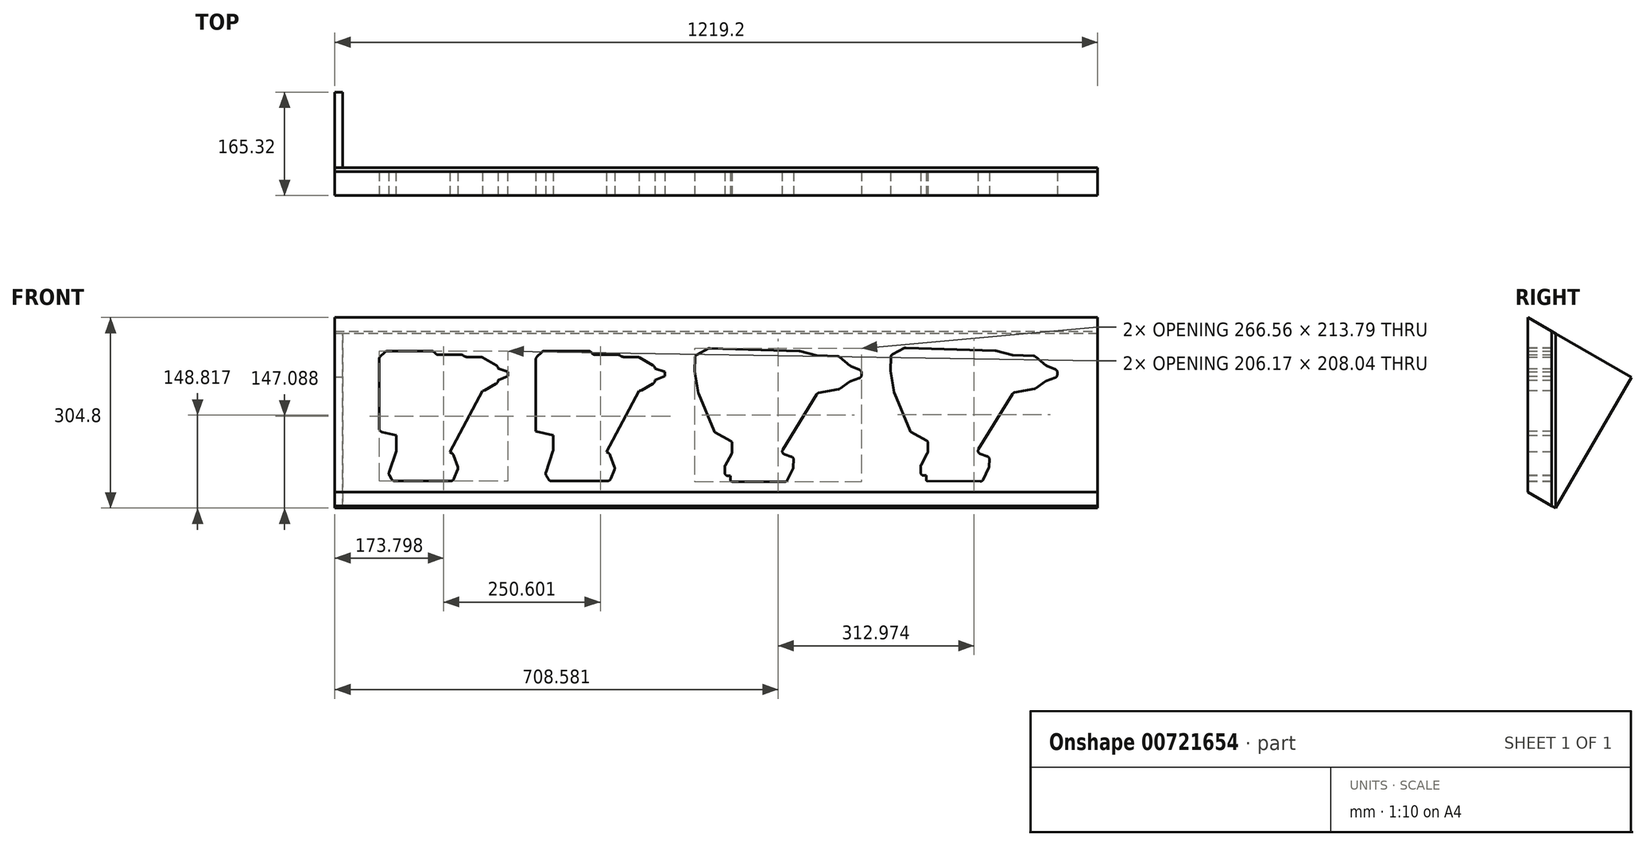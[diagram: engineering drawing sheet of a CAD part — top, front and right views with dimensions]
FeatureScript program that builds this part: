
annotation { "Feature Type Name" : "Feature", "Feature Type Description" : "" }
export const myFeature = defineFeature(function(context is Context, id is Id, definition is map)
    precondition{}
    {
        {
            var Q0;
            Q0=qCreatedBy(makeId("Front.planeOp"),FACE);
            var sketch = newSketch(context, id + "F0", { "sketchPlane" : qUnion([Q0])});
            skLineSegment(sketch, "E0", {"start": v(-3.88, -145.07) * mm, "end": v(92.56, -145.07) * mm});
            skLineSegment(sketch, "E1", {"start": v(92.56, -145.07) * mm, "end": v(100.9, -124.9) * mm});
            skLineSegment(sketch, "E2", {"start": v(100.9, -124.9) * mm, "end": v(92.56, -101.68) * mm});
            skLineSegment(sketch, "E3", {"start": v(92.56, -101.68) * mm, "end": v(82.48, -94.66) * mm});
            skLineSegment(sketch, "E4", {"start": v(82.48, -94.66) * mm, "end": v(58.37, -94.66) * mm});
            skLineSegment(sketch, "E5", {"start": v(58.37, -94.66) * mm, "end": v(63.63, -76.69) * mm});
            skLineSegment(sketch, "E6", {"start": v(63.63, -76.69) * mm, "end": v(66.7, -51.27) * mm});
            skLineSegment(sketch, "E7", {"start": v(66.7, -51.27) * mm, "end": v(92.56, -40.74) * mm});
            skLineSegment(sketch, "E8", {"start": v(92.56, -40.74) * mm, "end": v(88.62, -21.46) * mm});
            skLineSegment(sketch, "E9", {"start": v(88.62, -21.46) * mm, "end": v(105.71, -13.13) * mm});
            skLineSegment(sketch, "E10", {"start": v(105.71, -13.13) * mm, "end": v(112.29, -3.05) * mm});
            skLineSegment(sketch, "E11", {"start": v(112.29, -3.05) * mm, "end": v(141.66, -0.42) * mm});
            skLineSegment(sketch, "E12", {"start": v(141.66, -0.42) * mm, "end": v(164.84, 12.68) * mm});
            skLineSegment(sketch, "E13", {"start": v(164.84, 12.68) * mm, "end": v(164.84, 38.14) * mm});
            skLineSegment(sketch, "E14", {"start": v(164.84, 38.14) * mm, "end": v(138.25, 53.59) * mm});
            skLineSegment(sketch, "E15", {"start": v(138.25, 53.59) * mm, "end": v(112.38, 53.59) * mm});
            skLineSegment(sketch, "E16", {"start": v(112.38, 53.59) * mm, "end": v(107.55, 57) * mm});
            skLineSegment(sketch, "E17", {"start": v(107.55, 57) * mm, "end": v(65.77, 57) * mm});
            skLineSegment(sketch, "E18", {"start": v(65.77, 57) * mm, "end": v(61.79, 62.97) * mm});
            skLineSegment(sketch, "E19", {"start": v(61.79, 62.97) * mm, "end": v(-14.67, 62.97) * mm});
            skLineSegment(sketch, "E20", {"start": v(-14.67, 62.97) * mm, "end": v(-25.66, 51.99) * mm});
            skLineSegment(sketch, "E21", {"start": v(-25.66, 51.99) * mm, "end": v(-25.66, 17.9) * mm});
            skLineSegment(sketch, "E22", {"start": v(-25.66, 17.9) * mm, "end": v(-13.25, -15.48) * mm});
            skLineSegment(sketch, "E23", {"start": v(-13.25, -15.48) * mm, "end": v(10.62, -20.03) * mm});
            skLineSegment(sketch, "E24", {"start": v(10.62, -20.03) * mm, "end": v(5.27, -48.11) * mm});
            skLineSegment(sketch, "E25", {"start": v(5.27, -48.11) * mm, "end": v(2.1, -72.04) * mm});
            skLineSegment(sketch, "E26", {"start": v(2.1, -72.04) * mm, "end": v(2.1, -95.92) * mm});
            skLineSegment(sketch, "E27", {"start": v(2.1, -95.92) * mm, "end": v(-10.38, -133.46) * mm});
            skLineSegment(sketch, "E28", {"start": v(-10.38, -133.46) * mm, "end": v(-3.88, -145.07) * mm});
            skLineSegment(sketch, "E29.bottom", {"start": v(-96.37, 116.66) * mm, "end": v(1122.83, 116.66) * mm});
            skLineSegment(sketch, "E29.top", {"start": v(-96.37, -188.14) * mm, "end": v(1122.83, -188.14) * mm});
            skLineSegment(sketch, "E29.left", {"start": v(-96.37, 116.66) * mm, "end": v(-96.37, -188.14) * mm});
            skLineSegment(sketch, "E29.right", {"start": v(1122.83, 116.66) * mm, "end": v(1122.83, -188.14) * mm});
            skLineSegment(sketch, "E30", {"start": v(164.84, 35.17) * mm, "end": v(180.52, 29.83) * mm});
            skLineSegment(sketch, "E31", {"start": v(180.52, 29.83) * mm, "end": v(180.52, 22.7) * mm});
            skLineSegment(sketch, "E32", {"start": v(180.52, 22.7) * mm, "end": v(164.84, 16.26) * mm});
            skSolve(sketch);
        }
        {
            var Q0;
            Q0 = qSketchRegion(id + "F0", true);
            extrude(context, id + "F1", {"entities" : qUnion([Q0]), "depth" : 38.1 * mm, "offsetDistance" : 25.4 * mm});
        }
        {
            var Q0;
            Q0=makeQuery(id+"F1.opExtrude","SWEPT_EDGE",EDGE,{"disambiguationData":[OSD([sQuery(id+"F0.wireOp",EDGE,"E23"),sQuery(id+"F0.wireOp",EDGE,"E24")])]});
            var Q1;
            Q1=makeQuery(id+"F1.opExtrude","SWEPT_EDGE",EDGE,{"disambiguationData":[OSD([sQuery(id+"F0.wireOp",EDGE,"E22"),sQuery(id+"F0.wireOp",EDGE,"E23")])]});
            var Q2;
            Q2=makeQuery(id+"F1.opExtrude","SWEPT_EDGE",EDGE,{"disambiguationData":[OSD([sQuery(id+"F0.wireOp",EDGE,"E21"),sQuery(id+"F0.wireOp",EDGE,"E22")])]});
            var Q3;
            Q3=makeQuery(id+"F1.opExtrude","SWEPT_EDGE",EDGE,{"disambiguationData":[OSD([sQuery(id+"F0.wireOp",EDGE,"E20"),sQuery(id+"F0.wireOp",EDGE,"E21")])]});
            var Q4;
            Q4=makeQuery(id+"F1.opExtrude","SWEPT_EDGE",EDGE,{"disambiguationData":[OSD([sQuery(id+"F0.wireOp",EDGE,"E19"),sQuery(id+"F0.wireOp",EDGE,"E20")])]});
            var Q5;
            Q5=makeQuery(id+"F1.opExtrude","SWEPT_EDGE",EDGE,{"disambiguationData":[OSD([sQuery(id+"F0.wireOp",EDGE,"E18"),sQuery(id+"F0.wireOp",EDGE,"E19")])]});
            var Q6;
            Q6=makeQuery(id+"F1.opExtrude","SWEPT_EDGE",EDGE,{"disambiguationData":[OSD([sQuery(id+"F0.wireOp",EDGE,"E17"),sQuery(id+"F0.wireOp",EDGE,"E18")])]});
            var Q7;
            Q7=makeQuery(id+"F1.opExtrude","SWEPT_EDGE",EDGE,{"disambiguationData":[OSD([sQuery(id+"F0.wireOp",EDGE,"E16"),sQuery(id+"F0.wireOp",EDGE,"E17")])]});
            var Q8;
            Q8=makeQuery(id+"F1.opExtrude","SWEPT_EDGE",EDGE,{"disambiguationData":[OSD([sQuery(id+"F0.wireOp",EDGE,"E15"),sQuery(id+"F0.wireOp",EDGE,"E16")])]});
            var Q9;
            Q9=makeQuery(id+"F1.opExtrude","SWEPT_EDGE",EDGE,{"disambiguationData":[OSD([sQuery(id+"F0.wireOp",EDGE,"E14"),sQuery(id+"F0.wireOp",EDGE,"E15")])]});
            var Q10;
            Q10=makeQuery(id+"F1.opExtrude","SWEPT_EDGE",EDGE,{"disambiguationData":[OSD([sQuery(id+"F0.wireOp",EDGE,"E13"),sQuery(id+"F0.wireOp",EDGE,"E14")])]});
            var Q11;
            Q11=makeQuery(id+"F1.opExtrude","SWEPT_EDGE",EDGE,{"disambiguationData":[OSD([sQuery(id+"F0.wireOp",EDGE,"E12"),sQuery(id+"F0.wireOp",EDGE,"E13")])]});
            var Q12;
            Q12=makeQuery(id+"F1.opExtrude","SWEPT_EDGE",EDGE,{"disambiguationData":[OSD([sQuery(id+"F0.wireOp",EDGE,"E11"),sQuery(id+"F0.wireOp",EDGE,"E12")])]});
            var Q13;
            Q13=makeQuery(id+"F1.opExtrude","SWEPT_EDGE",EDGE,{"disambiguationData":[OSD([sQuery(id+"F0.wireOp",EDGE,"E10"),sQuery(id+"F0.wireOp",EDGE,"E11")])]});
            var Q14;
            Q14=makeQuery(id+"F1.opExtrude","SWEPT_EDGE",EDGE,{"disambiguationData":[OSD([sQuery(id+"F0.wireOp",EDGE,"E9"),sQuery(id+"F0.wireOp",EDGE,"E10")])]});
            var Q15;
            Q15=makeQuery(id+"F1.opExtrude","SWEPT_EDGE",EDGE,{"disambiguationData":[OSD([sQuery(id+"F0.wireOp",EDGE,"E8"),sQuery(id+"F0.wireOp",EDGE,"E9")])]});
            var Q16;
            Q16=makeQuery(id+"F1.opExtrude","SWEPT_EDGE",EDGE,{"disambiguationData":[OSD([sQuery(id+"F0.wireOp",EDGE,"E7"),sQuery(id+"F0.wireOp",EDGE,"E8")])]});
            var Q17;
            Q17=makeQuery(id+"F1.opExtrude","SWEPT_EDGE",EDGE,{"disambiguationData":[OSD([sQuery(id+"F0.wireOp",EDGE,"E6"),sQuery(id+"F0.wireOp",EDGE,"E7")])]});
            var Q18;
            Q18=makeQuery(id+"F1.opExtrude","SWEPT_EDGE",EDGE,{"disambiguationData":[OSD([sQuery(id+"F0.wireOp",EDGE,"E5"),sQuery(id+"F0.wireOp",EDGE,"E6")])]});
            var Q19;
            Q19=makeQuery(id+"F1.opExtrude","SWEPT_EDGE",EDGE,{"disambiguationData":[OSD([sQuery(id+"F0.wireOp",EDGE,"E4"),sQuery(id+"F0.wireOp",EDGE,"E5")])]});
            var Q20;
            Q20=makeQuery(id+"F1.opExtrude","SWEPT_EDGE",EDGE,{"disambiguationData":[OSD([sQuery(id+"F0.wireOp",EDGE,"E2"),sQuery(id+"F0.wireOp",EDGE,"E3")])]});
            var Q21;
            Q21=makeQuery(id+"F1.opExtrude","SWEPT_EDGE",EDGE,{"disambiguationData":[OSD([sQuery(id+"F0.wireOp",EDGE,"E1"),sQuery(id+"F0.wireOp",EDGE,"E2")])]});
            var Q22;
            Q22=makeQuery(id+"F1.opExtrude","SWEPT_EDGE",EDGE,{"disambiguationData":[OSD([sQuery(id+"F0.wireOp",EDGE,"E3"),sQuery(id+"F0.wireOp",EDGE,"E4")])]});
            var Q23;
            Q23=makeQuery(id+"F1.opExtrude","SWEPT_EDGE",EDGE,{"disambiguationData":[OSD([sQuery(id+"F0.wireOp",EDGE,"E0"),sQuery(id+"F0.wireOp",EDGE,"E1")])]});
            var Q24;
            Q24=makeQuery(id+"F1.opExtrude","SWEPT_EDGE",EDGE,{"disambiguationData":[OSD([sQuery(id+"F0.wireOp",EDGE,"E0"),sQuery(id+"F0.wireOp",EDGE,"E28")])]});
            var Q25;
            Q25=makeQuery(id+"F1.opExtrude","SWEPT_EDGE",EDGE,{"disambiguationData":[OSD([sQuery(id+"F0.wireOp",EDGE,"E27"),sQuery(id+"F0.wireOp",EDGE,"E28")])]});
            var Q26;
            Q26=makeQuery(id+"F1.opExtrude","SWEPT_EDGE",EDGE,{"disambiguationData":[OSD([sQuery(id+"F0.wireOp",EDGE,"E26"),sQuery(id+"F0.wireOp",EDGE,"E27")])]});
            var Q27;
            Q27=makeQuery(id+"F1.opExtrude","SWEPT_EDGE",EDGE,{"disambiguationData":[OSD([sQuery(id+"F0.wireOp",EDGE,"E25"),sQuery(id+"F0.wireOp",EDGE,"E26")])]});
            var Q28;
            Q28=makeQuery(id+"F1.opExtrude","SWEPT_EDGE",EDGE,{"disambiguationData":[OSD([sQuery(id+"F0.wireOp",EDGE,"E24"),sQuery(id+"F0.wireOp",EDGE,"E25")])]});
            fillet(context, id + "F2", {"entities" : qUnion([Q0, Q1, Q2, Q3, Q4, Q5, Q6, Q7, Q8, Q9, Q10, Q11, Q12, Q13, Q14, Q15, Q16, Q17, Q18, Q19, Q20, Q21, Q22, Q23, Q24, Q25, Q26, Q27, Q28]), "radius" : 6.35 * mm, "tangentPropagation" : true, "allowEdgeOverflow" : false});
        }
        {
            var Q0;
            Q0=makeQuery(id+"F1.opExtrude","CAP_FACE",FACE,{"disambiguationData":[OSD([sQuery(id+"F0.wireOp",EDGE,"E0"),sQuery(id+"F0.wireOp",EDGE,"E1"),sQuery(id+"F0.wireOp",EDGE,"E2"),sQuery(id+"F0.wireOp",EDGE,"E3"),sQuery(id+"F0.wireOp",EDGE,"E4"),sQuery(id+"F0.wireOp",EDGE,"E5"),sQuery(id+"F0.wireOp",EDGE,"E6"),sQuery(id+"F0.wireOp",EDGE,"E7"),sQuery(id+"F0.wireOp",EDGE,"E8"),sQuery(id+"F0.wireOp",EDGE,"E9"),sQuery(id+"F0.wireOp",EDGE,"E10"),sQuery(id+"F0.wireOp",EDGE,"E11"),sQuery(id+"F0.wireOp",EDGE,"E12"),sQuery(id+"F0.wireOp",EDGE,"E13"),sQuery(id+"F0.wireOp",EDGE,"E14"),sQuery(id+"F0.wireOp",EDGE,"E15"),sQuery(id+"F0.wireOp",EDGE,"E16"),sQuery(id+"F0.wireOp",EDGE,"E17"),sQuery(id+"F0.wireOp",EDGE,"E18"),sQuery(id+"F0.wireOp",EDGE,"E19"),sQuery(id+"F0.wireOp",EDGE,"E20"),sQuery(id+"F0.wireOp",EDGE,"E21"),sQuery(id+"F0.wireOp",EDGE,"E22"),sQuery(id+"F0.wireOp",EDGE,"E23"),sQuery(id+"F0.wireOp",EDGE,"E24"),sQuery(id+"F0.wireOp",EDGE,"E25"),sQuery(id+"F0.wireOp",EDGE,"E26"),sQuery(id+"F0.wireOp",EDGE,"E27"),sQuery(id+"F0.wireOp",EDGE,"E28"),sQuery(id+"F0.wireOp",EDGE,"E29.bottom"),sQuery(id+"F0.wireOp",EDGE,"E29.top"),sQuery(id+"F0.wireOp",EDGE,"E29.left"),sQuery(id+"F0.wireOp",EDGE,"E29.right")])],"isStart":false});
            var sketch = newSketch(context, id + "F3", { "sketchPlane" : qUnion([Q0])});
            skLineSegment(sketch, "E33", {"start": v(-25.66, 19.04) * mm, "end": v(-25.66, -65.36) * mm});
            skLineSegment(sketch, "E34", {"start": v(87.5, -98.16) * mm, "end": v(139.63, -0.6) * mm});
            skLineSegment(sketch, "E35.0", {"start": v(-0.16, -145.07) * mm, "end": v(88.31, -145.07) * mm});
            skArc(sketch, "E35.1", {"start": v(-0.16, -145.07) * mm, "mid": v(-3.37, -144.2) * mm, "end": v(-5.7, -141.83) * mm});
            skLineSegment(sketch, "E35.2", {"start": v(-9, -135.9) * mm, "end": v(-5.7, -141.83) * mm});
            skArc(sketch, "E35.3", {"start": v(-9, -135.9) * mm, "mid": v(-9.8, -133.4) * mm, "end": v(-9.5, -130.8) * mm});
            skLineSegment(sketch, "E35.4", {"start": v(1.77, -96.9) * mm, "end": v(-9.5, -130.8) * mm});
            skArc(sketch, "E35.5", {"start": v(94.18, -141.15) * mm, "mid": v(91.84, -144) * mm, "end": v(88.31, -145.07) * mm});
            skLineSegment(sketch, "E35.6", {"start": v(94.18, -141.15) * mm, "end": v(99.96, -127.17) * mm});
            skArc(sketch, "E35.7", {"start": v(100.06, -122.6) * mm, "mid": v(100.44, -124.9) * mm, "end": v(99.96, -127.17) * mm});
            skLineSegment(sketch, "E35.8", {"start": v(100.06, -122.6) * mm, "end": v(93.25, -103.59) * mm});
            skLineSegment(sketch, "E35.9", {"start": v(90.9, -100.52) * mm, "end": v(87.5, -98.16) * mm});
            skArc(sketch, "E35.10", {"start": v(90.9, -100.52) * mm, "mid": v(92.31, -101.87) * mm, "end": v(93.25, -103.59) * mm});
            skLineSegment(sketch, "E35.12", {"start": v(2.1, -72.46) * mm, "end": v(2.1, -94.9) * mm});
            skLineSegment(sketch, "E35.13", {"start": v(142.85, 0.26) * mm, "end": v(161.61, 10.85) * mm});
            skArc(sketch, "E35.14", {"start": v(164.84, 16.26) * mm, "mid": v(163.95, 13.13) * mm, "end": v(161.61, 10.85) * mm});
            skLineSegment(sketch, "E35.15", {"start": v(180.52, 22.7) * mm, "end": v(164.84, 16.26) * mm});
            skLineSegment(sketch, "E35.16", {"start": v(180.52, 29.83) * mm, "end": v(180.52, 22.7) * mm});
            skLineSegment(sketch, "E35.17", {"start": v(164.84, 35.17) * mm, "end": v(180.52, 29.83) * mm});
            skArc(sketch, "E35.18", {"start": v(161.72, 39.96) * mm, "mid": v(163.85, 37.93) * mm, "end": v(164.84, 35.17) * mm});
            skLineSegment(sketch, "E35.19", {"start": v(161.72, 39.96) * mm, "end": v(139.73, 52.73) * mm});
            skArc(sketch, "E35.20", {"start": v(136.54, 53.59) * mm, "mid": v(138.19, 53.37) * mm, "end": v(139.73, 52.73) * mm});
            skLineSegment(sketch, "E35.21", {"start": v(136.54, 53.59) * mm, "end": v(114.4, 53.59) * mm});
            skArc(sketch, "E35.22", {"start": v(110.73, 54.75) * mm, "mid": v(112.48, 53.89) * mm, "end": v(114.4, 53.59) * mm});
            skLineSegment(sketch, "E35.23", {"start": v(110.73, 54.75) * mm, "end": v(109.2, 55.84) * mm});
            skArc(sketch, "E35.24", {"start": v(105.53, 57) * mm, "mid": v(107.45, 56.7) * mm, "end": v(109.2, 55.84) * mm});
            skLineSegment(sketch, "E35.26", {"start": v(105.53, 57) * mm, "end": v(69.16, 57) * mm});
            skPoint(sketch, "E35.27", {"position": v(92.31, -101.87) * mm});
            skArc(sketch, "E36.0", {"start": v(63.88, 59.83) * mm, "mid": v(66.17, 57.75) * mm, "end": v(69.16, 57) * mm});
            skArc(sketch, "E36.1", {"start": v(58.39, 62.97) * mm, "mid": v(61.38, 62.22) * mm, "end": v(63.67, 60.14) * mm});
            skLineSegment(sketch, "E36.2", {"start": v(58.39, 62.97) * mm, "end": v(-12.04, 62.97) * mm});
            skPoint(sketch, "E36.3", {"position": v(-16.53, 61.1) * mm});
            skLineSegment(sketch, "E36.4", {"start": v(-16.53, 61.1) * mm, "end": v(-23.8, 53.85) * mm});
            skArc(sketch, "E36.5", {"start": v(-16.53, 61.1) * mm, "mid": v(-14.47, 62.49) * mm, "end": v(-12.04, 62.97) * mm});
            skLineSegment(sketch, "E36.6", {"start": v(-25.66, 49.35) * mm, "end": v(-25.66, 19.04) * mm});
            skArc(sketch, "E36.7", {"start": v(-25.66, 49.35) * mm, "mid": v(-25.18, 51.78) * mm, "end": v(-23.8, 53.85) * mm});
            skPoint(sketch, "E37.orphan", {"position": v(84.11, -95.8) * mm});
            skLineSegment(sketch, "E38", {"start": v(2.15, -71.63) * mm, "end": v(-25.66, -65.36) * mm});
            skPoint(sketch, "E39.0", {"position": v(2.01, -95.9) * mm});
            skArc(sketch, "E40.0", {"start": v(1.77, -96.9) * mm, "mid": v(2.01, -95.9) * mm, "end": v(2.1, -94.9) * mm});
            skArc(sketch, "E41.2", {"start": v(2.1, -72.46) * mm, "mid": v(2.1, -72.05) * mm, "end": v(2.15, -71.63) * mm});
            skArc(sketch, "E42.0", {"start": v(142.85, 0.26) * mm, "mid": v(141.61, -0.28) * mm, "end": v(140.3, -0.54) * mm});
            skLineSegment(sketch, "E42.1", {"start": v(139.63, -0.6) * mm, "end": v(140.3, -0.54) * mm});
            skPoint(sketch, "E43.orphan", {"position": v(115.36, -2.77) * mm});
            skLineSegment(sketch, "E44.0", {"start": v(63.88, 59.83) * mm, "end": v(63.67, 60.14) * mm});
            skLineSegment(sketch, "E45", {"start": v(-85.76, -145.07) * mm, "end": v(1133.44, -145.07) * mm, "construction": true});
            skLineSegment(sketch, "E46", {"start": v(224.94, 19.04) * mm, "end": v(224.94, -65.36) * mm});
            skLineSegment(sketch, "E47", {"start": v(338.1, -98.16) * mm, "end": v(390.23, -0.6) * mm});
            skLineSegment(sketch, "E48.0", {"start": v(250.45, -145.07) * mm, "end": v(338.91, -145.07) * mm});
            skArc(sketch, "E48.1", {"start": v(250.45, -145.07) * mm, "mid": v(247.23, -144.2) * mm, "end": v(244.9, -141.83) * mm});
            skLineSegment(sketch, "E48.2", {"start": v(241.6, -135.9) * mm, "end": v(244.9, -141.83) * mm});
            skArc(sketch, "E48.3", {"start": v(241.6, -135.9) * mm, "mid": v(240.8, -133.4) * mm, "end": v(241.1, -130.8) * mm});
            skLineSegment(sketch, "E48.4", {"start": v(252.37, -96.9) * mm, "end": v(241.1, -130.8) * mm});
            skArc(sketch, "E48.5", {"start": v(344.78, -141.15) * mm, "mid": v(342.45, -144) * mm, "end": v(338.91, -145.07) * mm});
            skLineSegment(sketch, "E48.6", {"start": v(344.78, -141.15) * mm, "end": v(350.56, -127.17) * mm});
            skArc(sketch, "E48.7", {"start": v(350.66, -122.6) * mm, "mid": v(351.04, -124.9) * mm, "end": v(350.56, -127.17) * mm});
            skLineSegment(sketch, "E48.8", {"start": v(350.66, -122.6) * mm, "end": v(343.85, -103.59) * mm});
            skLineSegment(sketch, "E48.9", {"start": v(341.5, -100.52) * mm, "end": v(338.1, -98.16) * mm});
            skArc(sketch, "E48.10", {"start": v(341.5, -100.52) * mm, "mid": v(342.91, -101.87) * mm, "end": v(343.85, -103.59) * mm});
            skLineSegment(sketch, "E48.12", {"start": v(252.7, -72.46) * mm, "end": v(252.7, -94.9) * mm});
            skLineSegment(sketch, "E48.13", {"start": v(393.45, 0.26) * mm, "end": v(412.22, 10.85) * mm});
            skArc(sketch, "E48.14", {"start": v(415.44, 16.26) * mm, "mid": v(414.55, 13.13) * mm, "end": v(412.22, 10.85) * mm});
            skLineSegment(sketch, "E48.15", {"start": v(431.12, 22.7) * mm, "end": v(415.44, 16.26) * mm});
            skLineSegment(sketch, "E48.16", {"start": v(431.12, 29.83) * mm, "end": v(431.12, 22.7) * mm});
            skLineSegment(sketch, "E48.17", {"start": v(415.44, 35.17) * mm, "end": v(431.12, 29.83) * mm});
            skArc(sketch, "E48.18", {"start": v(412.32, 39.96) * mm, "mid": v(414.45, 37.93) * mm, "end": v(415.44, 35.17) * mm});
            skLineSegment(sketch, "E48.19", {"start": v(412.32, 39.96) * mm, "end": v(390.33, 52.73) * mm});
            skArc(sketch, "E48.20", {"start": v(387.14, 53.59) * mm, "mid": v(388.79, 53.37) * mm, "end": v(390.33, 52.73) * mm});
            skLineSegment(sketch, "E48.21", {"start": v(387.14, 53.59) * mm, "end": v(365, 53.59) * mm});
            skArc(sketch, "E48.22", {"start": v(361.33, 54.75) * mm, "mid": v(363.08, 53.89) * mm, "end": v(365, 53.59) * mm});
            skLineSegment(sketch, "E48.23", {"start": v(361.33, 54.75) * mm, "end": v(359.8, 55.84) * mm});
            skArc(sketch, "E48.24", {"start": v(356.13, 57) * mm, "mid": v(358.05, 56.7) * mm, "end": v(359.8, 55.84) * mm});
            skLineSegment(sketch, "E48.26", {"start": v(356.13, 57) * mm, "end": v(319.76, 57) * mm});
            skPoint(sketch, "E48.27", {"position": v(342.9, -101.87) * mm});
            skArc(sketch, "E49.0", {"start": v(314.48, 59.83) * mm, "mid": v(316.77, 57.75) * mm, "end": v(319.76, 57) * mm});
            skArc(sketch, "E49.1", {"start": v(308.99, 62.97) * mm, "mid": v(311.98, 62.22) * mm, "end": v(314.27, 60.14) * mm});
            skLineSegment(sketch, "E49.2", {"start": v(308.99, 62.97) * mm, "end": v(238.56, 62.97) * mm});
            skPoint(sketch, "E49.3", {"position": v(234.07, 61.1) * mm});
            skLineSegment(sketch, "E49.4", {"start": v(234.07, 61.1) * mm, "end": v(226.8, 53.85) * mm});
            skArc(sketch, "E49.5", {"start": v(234.07, 61.1) * mm, "mid": v(236.13, 62.49) * mm, "end": v(238.56, 62.97) * mm});
            skLineSegment(sketch, "E49.6", {"start": v(224.94, 49.35) * mm, "end": v(224.94, 19.04) * mm});
            skArc(sketch, "E49.7", {"start": v(224.94, 49.35) * mm, "mid": v(225.43, 51.79) * mm, "end": v(226.8, 53.85) * mm});
            skPoint(sketch, "E50.orphan", {"position": v(334.71, -95.8) * mm});
            skLineSegment(sketch, "E51", {"start": v(252.75, -71.63) * mm, "end": v(224.94, -65.36) * mm});
            skPoint(sketch, "E52.0", {"position": v(252.61, -95.9) * mm});
            skArc(sketch, "E53.0", {"start": v(252.37, -96.9) * mm, "mid": v(252.61, -95.9) * mm, "end": v(252.7, -94.9) * mm});
            skArc(sketch, "E54.2", {"start": v(252.7, -72.46) * mm, "mid": v(252.71, -72.05) * mm, "end": v(252.75, -71.63) * mm});
            skArc(sketch, "E55.0", {"start": v(393.45, 0.26) * mm, "mid": v(392.21, -0.28) * mm, "end": v(390.9, -0.54) * mm});
            skLineSegment(sketch, "E55.1", {"start": v(390.23, -0.6) * mm, "end": v(390.9, -0.54) * mm});
            skPoint(sketch, "E56.orphan", {"position": v(365.96, -2.77) * mm});
            skLineSegment(sketch, "E57.0", {"start": v(314.48, 59.83) * mm, "end": v(314.27, 60.14) * mm});
            skLineSegment(sketch, "E58.1", {"start": v(503.42, 67.57) * mm, "end": v(645.87, 62.84) * mm});
            skArc(sketch, "E58.2", {"start": v(500.9, 67) * mm, "mid": v(502.12, 67.45) * mm, "end": v(503.42, 67.57) * mm});
            skLineSegment(sketch, "E58.3", {"start": v(482.38, 57.35) * mm, "end": v(500.9, 67) * mm});
            skArc(sketch, "E58.4", {"start": v(479.65, 53.02) * mm, "mid": v(480.43, 55.56) * mm, "end": v(482.38, 57.35) * mm});
            skLineSegment(sketch, "E58.5", {"start": v(478.93, 31.35) * mm, "end": v(479.65, 53.02) * mm});
            skLineSegment(sketch, "E58.6", {"start": v(646.97, 62.69) * mm, "end": v(673.62, 55.83) * mm});
            skArc(sketch, "E58.7", {"start": v(645.87, 62.84) * mm, "mid": v(646.42, 62.8) * mm, "end": v(646.97, 62.69) * mm});
            skArc(sketch, "E58.8", {"start": v(673.62, 55.83) * mm, "mid": v(674.16, 55.72) * mm, "end": v(674.71, 55.67) * mm});
            skLineSegment(sketch, "E58.9", {"start": v(674.71, 55.67) * mm, "end": v(707.37, 54.59) * mm});
            skArc(sketch, "E58.10", {"start": v(707.37, 54.59) * mm, "mid": v(708.98, 54.27) * mm, "end": v(710.4, 53.45) * mm});
            skLineSegment(sketch, "E58.11", {"start": v(710.4, 53.45) * mm, "end": v(727.44, 39.6) * mm});
            skArc(sketch, "E58.12", {"start": v(727.44, 39.6) * mm, "mid": v(728.01, 39.19) * mm, "end": v(728.64, 38.87) * mm});
            skLineSegment(sketch, "E58.13", {"start": v(728.64, 38.87) * mm, "end": v(742.42, 32.94) * mm});
            skArc(sketch, "E58.14", {"start": v(742.42, 32.94) * mm, "mid": v(744.7, 31) * mm, "end": v(745.49, 28.1) * mm});
            skLineSegment(sketch, "E58.15", {"start": v(745.49, 28.1) * mm, "end": v(745.36, 24.17) * mm});
            skArc(sketch, "E58.16", {"start": v(745.36, 24.17) * mm, "mid": v(744.38, 21.34) * mm, "end": v(741.98, 19.55) * mm});
            skLineSegment(sketch, "E58.17", {"start": v(741.98, 19.55) * mm, "end": v(727.83, 14.55) * mm});
            skArc(sketch, "E58.18", {"start": v(727.83, 14.55) * mm, "mid": v(727.19, 14.27) * mm, "end": v(726.59, 13.9) * mm});
            skLineSegment(sketch, "E58.19", {"start": v(726.59, 13.9) * mm, "end": v(710.58, 2.57) * mm});
            skArc(sketch, "E58.20", {"start": v(710.58, 2.57) * mm, "mid": v(709.61, 2.03) * mm, "end": v(708.56, 1.71) * mm});
            skLineSegment(sketch, "E58.21", {"start": v(708.56, 1.71) * mm, "end": v(677.11, -4.02) * mm});
            skArc(sketch, "E58.22", {"start": v(677.11, -4.02) * mm, "mid": v(675.15, -4.83) * mm, "end": v(673.7, -6.36) * mm});
            skLineSegment(sketch, "E58.23", {"start": v(619.56, -94.7) * mm, "end": v(673.7, -6.36) * mm});
            skArc(sketch, "E58.24", {"start": v(619.56, -94.7) * mm, "mid": v(619.12, -99.1) * mm, "end": v(622.28, -102.18) * mm});
            skLineSegment(sketch, "E58.25", {"start": v(622.28, -102.18) * mm, "end": v(633.44, -105.92) * mm});
            skArc(sketch, "E58.26", {"start": v(633.44, -105.92) * mm, "mid": v(636, -107.83) * mm, "end": v(636.9, -110.9) * mm});
            skLineSegment(sketch, "E58.27", {"start": v(636.9, -110.9) * mm, "end": v(636.53, -122.23) * mm});
            skLineSegment(sketch, "E58.28", {"start": v(636.03, -124.25) * mm, "end": v(626.9, -143.33) * mm});
            skArc(sketch, "E58.29", {"start": v(636.53, -122.23) * mm, "mid": v(636.39, -123.27) * mm, "end": v(636.03, -124.25) * mm});
            skArc(sketch, "E58.30", {"start": v(626.9, -143.33) * mm, "mid": v(625.01, -145.44) * mm, "end": v(622.29, -146.22) * mm});
            skLineSegment(sketch, "E58.31", {"start": v(622.29, -146.22) * mm, "end": v(538.27, -145.73) * mm});
            skArc(sketch, "E58.32", {"start": v(538.27, -145.73) * mm, "mid": v(536.75, -145.1) * mm, "end": v(536.13, -143.56) * mm});
            skLineSegment(sketch, "E58.33", {"start": v(536.13, -143.56) * mm, "end": v(536.17, -136.78) * mm});
            skLineSegment(sketch, "E58.34", {"start": v(536.17, -136.78) * mm, "end": v(532, -136.76) * mm});
            skArc(sketch, "E58.35", {"start": v(532, -136.76) * mm, "mid": v(528.41, -135.25) * mm, "end": v(526.95, -131.65) * mm});
            skLineSegment(sketch, "E58.36", {"start": v(526.95, -131.65) * mm, "end": v(527, -122.17) * mm});
            skArc(sketch, "E58.37", {"start": v(527, -122.17) * mm, "mid": v(527.17, -120.9) * mm, "end": v(527.64, -119.72) * mm});
            skLineSegment(sketch, "E58.38", {"start": v(527.64, -119.72) * mm, "end": v(537.65, -101.75) * mm});
            skArc(sketch, "E58.39", {"start": v(537.65, -101.75) * mm, "mid": v(538.1, -100.64) * mm, "end": v(538.29, -99.45) * mm});
            skLineSegment(sketch, "E58.40", {"start": v(538.29, -99.45) * mm, "end": v(538.76, -85.12) * mm});
            skArc(sketch, "E58.41", {"start": v(538.76, -85.12) * mm, "mid": v(538.09, -82.43) * mm, "end": v(536.1, -80.49) * mm});
            skLineSegment(sketch, "E58.42", {"start": v(536.1, -80.49) * mm, "end": v(512.08, -67.51) * mm});
            skArc(sketch, "E58.43", {"start": v(512.08, -67.51) * mm, "mid": v(510.72, -66.45) * mm, "end": v(509.8, -64.99) * mm});
            skLineSegment(sketch, "E58.44", {"start": v(509.8, -64.99) * mm, "end": v(485.02, -5.14) * mm});
            skLineSegment(sketch, "E58.45", {"start": v(484.7, -4.03) * mm, "end": v(479, 30.36) * mm});
            skArc(sketch, "E58.46", {"start": v(485.02, -5.14) * mm, "mid": v(484.83, -4.6) * mm, "end": v(484.7, -4.03) * mm});
            skArc(sketch, "E58.47", {"start": v(479, 30.36) * mm, "mid": v(478.94, 30.85) * mm, "end": v(478.93, 31.35) * mm});
            skPoint(sketch, "E58.48", {"position": v(636.39, -123.27) * mm});
            skLineSegment(sketch, "E59.1", {"start": v(816.4, 68.23) * mm, "end": v(958.84, 63.5) * mm});
            skArc(sketch, "E59.2", {"start": v(813.88, 67.66) * mm, "mid": v(815.1, 68.1) * mm, "end": v(816.4, 68.23) * mm});
            skLineSegment(sketch, "E59.3", {"start": v(795.36, 58.01) * mm, "end": v(813.88, 67.66) * mm});
            skArc(sketch, "E59.4", {"start": v(792.63, 53.68) * mm, "mid": v(793.4, 56.22) * mm, "end": v(795.36, 58.01) * mm});
            skLineSegment(sketch, "E59.5", {"start": v(791.9, 32.01) * mm, "end": v(792.63, 53.68) * mm});
            skLineSegment(sketch, "E59.6", {"start": v(959.94, 63.35) * mm, "end": v(986.6, 56.49) * mm});
            skArc(sketch, "E59.7", {"start": v(958.84, 63.5) * mm, "mid": v(959.4, 63.46) * mm, "end": v(959.94, 63.35) * mm});
            skArc(sketch, "E59.8", {"start": v(986.6, 56.49) * mm, "mid": v(987.13, 56.38) * mm, "end": v(987.69, 56.33) * mm});
            skLineSegment(sketch, "E59.9", {"start": v(987.69, 56.33) * mm, "end": v(1020.34, 55.25) * mm});
            skArc(sketch, "E59.10", {"start": v(1020.34, 55.25) * mm, "mid": v(1021.95, 54.93) * mm, "end": v(1023.38, 54.11) * mm});
            skLineSegment(sketch, "E59.11", {"start": v(1023.38, 54.11) * mm, "end": v(1040.41, 40.25) * mm});
            skArc(sketch, "E59.12", {"start": v(1040.41, 40.25) * mm, "mid": v(1040.99, 39.85) * mm, "end": v(1041.61, 39.53) * mm});
            skLineSegment(sketch, "E59.13", {"start": v(1041.61, 39.53) * mm, "end": v(1055.4, 33.6) * mm});
            skArc(sketch, "E59.14", {"start": v(1055.4, 33.6) * mm, "mid": v(1057.68, 31.65) * mm, "end": v(1058.46, 28.76) * mm});
            skLineSegment(sketch, "E59.15", {"start": v(1058.46, 28.76) * mm, "end": v(1058.33, 24.83) * mm});
            skArc(sketch, "E59.16", {"start": v(1058.33, 24.83) * mm, "mid": v(1057.36, 22) * mm, "end": v(1054.95, 20.2) * mm});
            skLineSegment(sketch, "E59.17", {"start": v(1054.95, 20.2) * mm, "end": v(1040.8, 15.2) * mm});
            skArc(sketch, "E59.18", {"start": v(1040.8, 15.2) * mm, "mid": v(1040.16, 14.93) * mm, "end": v(1039.56, 14.56) * mm});
            skLineSegment(sketch, "E59.19", {"start": v(1039.56, 14.56) * mm, "end": v(1023.55, 3.23) * mm});
            skArc(sketch, "E59.20", {"start": v(1023.55, 3.23) * mm, "mid": v(1022.59, 2.69) * mm, "end": v(1021.53, 2.37) * mm});
            skLineSegment(sketch, "E59.21", {"start": v(1021.53, 2.37) * mm, "end": v(990.09, -3.36) * mm});
            skArc(sketch, "E59.22", {"start": v(990.09, -3.36) * mm, "mid": v(988.13, -4.17) * mm, "end": v(986.67, -5.7) * mm});
            skLineSegment(sketch, "E59.23", {"start": v(932.53, -94.05) * mm, "end": v(986.67, -5.7) * mm});
            skArc(sketch, "E59.24", {"start": v(932.53, -94.05) * mm, "mid": v(932.1, -98.44) * mm, "end": v(935.25, -101.52) * mm});
            skLineSegment(sketch, "E59.25", {"start": v(935.25, -101.52) * mm, "end": v(946.42, -105.26) * mm});
            skArc(sketch, "E59.26", {"start": v(946.42, -105.26) * mm, "mid": v(948.97, -107.17) * mm, "end": v(949.88, -110.24) * mm});
            skLineSegment(sketch, "E59.27", {"start": v(949.88, -110.24) * mm, "end": v(949.5, -121.57) * mm});
            skLineSegment(sketch, "E59.28", {"start": v(949, -123.6) * mm, "end": v(939.87, -142.67) * mm});
            skArc(sketch, "E59.29", {"start": v(949.5, -121.57) * mm, "mid": v(949.36, -122.6) * mm, "end": v(949, -123.6) * mm});
            skArc(sketch, "E59.30", {"start": v(939.87, -142.67) * mm, "mid": v(937.98, -144.78) * mm, "end": v(935.26, -145.56) * mm});
            skLineSegment(sketch, "E59.31", {"start": v(935.26, -145.56) * mm, "end": v(851.25, -145.07) * mm});
            skArc(sketch, "E59.32", {"start": v(851.25, -145.07) * mm, "mid": v(849.72, -144.43) * mm, "end": v(849.1, -142.9) * mm});
            skLineSegment(sketch, "E59.33", {"start": v(849.1, -142.9) * mm, "end": v(849.14, -136.12) * mm});
            skLineSegment(sketch, "E59.34", {"start": v(849.14, -136.12) * mm, "end": v(844.97, -136.1) * mm});
            skArc(sketch, "E59.35", {"start": v(844.97, -136.1) * mm, "mid": v(841.39, -134.59) * mm, "end": v(839.92, -130.99) * mm});
            skLineSegment(sketch, "E59.36", {"start": v(839.92, -130.99) * mm, "end": v(839.97, -121.5) * mm});
            skArc(sketch, "E59.37", {"start": v(839.97, -121.5) * mm, "mid": v(840.14, -120.24) * mm, "end": v(840.62, -119.06) * mm});
            skLineSegment(sketch, "E59.38", {"start": v(840.62, -119.06) * mm, "end": v(850.62, -101.1) * mm});
            skArc(sketch, "E59.39", {"start": v(850.62, -101.1) * mm, "mid": v(851.08, -99.98) * mm, "end": v(851.26, -98.8) * mm});
            skLineSegment(sketch, "E59.40", {"start": v(851.26, -98.8) * mm, "end": v(851.73, -84.46) * mm});
            skArc(sketch, "E59.41", {"start": v(851.73, -84.46) * mm, "mid": v(851.06, -81.77) * mm, "end": v(849.07, -79.83) * mm});
            skLineSegment(sketch, "E59.42", {"start": v(849.07, -79.83) * mm, "end": v(825.05, -66.85) * mm});
            skArc(sketch, "E59.43", {"start": v(825.05, -66.85) * mm, "mid": v(823.7, -65.79) * mm, "end": v(822.77, -64.33) * mm});
            skLineSegment(sketch, "E59.44", {"start": v(822.77, -64.33) * mm, "end": v(798, -4.48) * mm});
            skLineSegment(sketch, "E59.45", {"start": v(797.67, -3.37) * mm, "end": v(791.97, 31.02) * mm});
            skArc(sketch, "E59.46", {"start": v(798, -4.48) * mm, "mid": v(797.8, -3.94) * mm, "end": v(797.67, -3.37) * mm});
            skArc(sketch, "E59.47", {"start": v(791.97, 31.02) * mm, "mid": v(791.92, 31.51) * mm, "end": v(791.9, 32.01) * mm});
            skPoint(sketch, "E59.48", {"position": v(949.36, -122.6) * mm});
            skSolve(sketch);
        }
        {
            var Q0;
            Q0 = qSketchRegion(id + "F3", true);
            extrude(context, id + "F4", {"entities" : qUnion([Q0]), "operationType" : NewBodyOperationType.REMOVE, "endBound" : BoundingType.THROUGH_ALL, "oppositeDirection" : true, "depth" : 25.4 * mm, "offsetDistance" : 25.4 * mm});
        }
        {
            var Q0;
            Q0=makeQuery(id+"F4.boolean.opBoolean","COPY",EDGE,{"derivedFrom":makeQuery(id+"F4.opExtrude","SWEPT_EDGE",EDGE,{"disambiguationData":[OSD([sQuery(id+"F0.wireOp",EDGE,"E3"),sQuery(id+"F3.wireOp",EDGE,"LrWBRPST-FAtx-mA5M-UwUX-kSxtfGQgJzkJ"),sQuery(id+"F3.wireOp",EDGE,"E34")])]})});
            var Q1;
            Q1=makeQuery(id+"F4.boolean.opBoolean","COPY",EDGE,{"derivedFrom":makeQuery(id+"F4.opExtrude","SWEPT_EDGE",EDGE,{"disambiguationData":[OSD([sQuery(id+"F0.wireOp",EDGE,"E11"),sQuery(id+"F3.wireOp",EDGE,"E34"),sQuery(id+"F3.wireOp",EDGE,"BqCTSTw9-kAuH-p5J8-t5J7-2BCGbxobdn49")])]})});
            var Q2;
            Q2=makeQuery(id+"F4.boolean.opBoolean","INTERSECT",EDGE,{"derivedFrom":[makeQuery(id+"F1.opExtrude","SWEPT_FACE",FACE,{"disambiguationData":[OSD([sQuery(id+"F0.wireOp",EDGE,"E25")])]}),makeQuery(id+"F4.opExtrude","SWEPT_FACE",FACE,{"disambiguationData":[OSD([sQuery(id+"F3.wireOp",EDGE,"nDux6Ryi-bpeC-6Rvh-rDcE-4Rn3OJgjeoaa")])]})]});
            var Q3;
            Q3=makeQuery(id+"F4.boolean.opBoolean","COPY",EDGE,{"derivedFrom":makeQuery(id+"F4.opExtrude","SWEPT_EDGE",EDGE,{"disambiguationData":[OSD([sQuery(id+"F3.wireOp",EDGE,"E33"),sQuery(id+"F3.wireOp",EDGE,"nDux6Ryi-bpeC-6Rvh-rDcE-4Rn3OJgjeoaa")])]})});
            fillet(context, id + "F5", {"entities" : qUnion([Q0, Q1, Q2, Q3]), "radius" : 6.35 * mm, "tangentPropagation" : true, "allowEdgeOverflow" : false});
        }
        {
            var Q0;
            Q0=makeQuery(id+"F1.opExtrude","CAP_FACE",FACE,{"disambiguationData":[OSD([sQuery(id+"F0.wireOp",EDGE,"E0"),sQuery(id+"F0.wireOp",EDGE,"E1"),sQuery(id+"F0.wireOp",EDGE,"E2"),sQuery(id+"F0.wireOp",EDGE,"E3"),sQuery(id+"F0.wireOp",EDGE,"E4"),sQuery(id+"F0.wireOp",EDGE,"E5"),sQuery(id+"F0.wireOp",EDGE,"E6"),sQuery(id+"F0.wireOp",EDGE,"E7"),sQuery(id+"F0.wireOp",EDGE,"E8"),sQuery(id+"F0.wireOp",EDGE,"E9"),sQuery(id+"F0.wireOp",EDGE,"E10"),sQuery(id+"F0.wireOp",EDGE,"E11"),sQuery(id+"F0.wireOp",EDGE,"E12"),sQuery(id+"F0.wireOp",EDGE,"E13"),sQuery(id+"F0.wireOp",EDGE,"E14"),sQuery(id+"F0.wireOp",EDGE,"E15"),sQuery(id+"F0.wireOp",EDGE,"E16"),sQuery(id+"F0.wireOp",EDGE,"E17"),sQuery(id+"F0.wireOp",EDGE,"E18"),sQuery(id+"F0.wireOp",EDGE,"E19"),sQuery(id+"F0.wireOp",EDGE,"E20"),sQuery(id+"F0.wireOp",EDGE,"E21"),sQuery(id+"F0.wireOp",EDGE,"E22"),sQuery(id+"F0.wireOp",EDGE,"E23"),sQuery(id+"F0.wireOp",EDGE,"E24"),sQuery(id+"F0.wireOp",EDGE,"E25"),sQuery(id+"F0.wireOp",EDGE,"E26"),sQuery(id+"F0.wireOp",EDGE,"E27"),sQuery(id+"F0.wireOp",EDGE,"E28"),sQuery(id+"F0.wireOp",EDGE,"E29.bottom"),sQuery(id+"F0.wireOp",EDGE,"E29.top"),sQuery(id+"F0.wireOp",EDGE,"E29.left"),sQuery(id+"F0.wireOp",EDGE,"E29.right"),sQuery(id+"F0.wireOp",EDGE,"E30"),sQuery(id+"F0.wireOp",EDGE,"E31"),sQuery(id+"F0.wireOp",EDGE,"E32")])],"isStart":true});
            var sketch = newSketch(context, id + "F6", { "sketchPlane" : qUnion([Q0])});
            skLineSegment(sketch, "E60.0", {"start": v(96.37, -188.14) * mm, "end": v(-1122.83, -188.14) * mm});
            skLineSegment(sketch, "E61.0", {"start": v(96.37, 116.66) * mm, "end": v(96.37, -188.14) * mm});
            skLineSegment(sketch, "E62.0", {"start": v(96.37, 116.66) * mm, "end": v(-1122.83, 116.66) * mm});
            skLineSegment(sketch, "E63.0", {"start": v(-1122.83, 116.66) * mm, "end": v(-1122.83, -188.14) * mm});
            skSolve(sketch);
        }
        {
            var Q0;
            Q0 = qSketchRegion(id + "F6", true);
            extrude(context, id + "F7", {"entities" : qUnion([Q0]), "depth" : 6.35 * mm, "offsetDistance" : 25.4 * mm});
        }
        {
            var Q0;
            Q0=makeQuery(id+"F1.opExtrude","SWEPT_FACE",FACE,{"disambiguationData":[OSD([sQuery(id+"F0.wireOp",EDGE,"E29.left")])]});
            var sketch = newSketch(context, id + "F8", { "sketchPlane" : qUnion([Q0])});
            skLineSegment(sketch, "E64", {"start": v(-127.22, 21.22) * mm, "end": v(-6.35, -188.14) * mm});
            skLineSegment(sketch, "E65", {"start": v(-6.35, -188.14) * mm, "end": v(-6.35, 91) * mm});
            skLineSegment(sketch, "E66", {"start": v(38.1, 116.66) * mm, "end": v(-127.22, 21.22) * mm});
            skSolve(sketch);
        }
        {
            var Q0;
            Q0 = qSketchRegion(id + "F8", true);
            extrude(context, id + "F9", {"entities" : qUnion([Q0]), "oppositeDirection" : true, "depth" : 12.7 * mm, "offsetDistance" : 25.4 * mm});
        }
        {
            var Q0;
            Q0=makeQuery(id+"F1.opExtrude","SWEPT_FACE",FACE,{"disambiguationData":[OSD([sQuery(id+"F0.wireOp",EDGE,"E29.left")])]});
            var sketch = newSketch(context, id + "F10", { "sketchPlane" : qUnion([Q0])});
            skPoint(sketch, "E67.0", {"position": v(-6.35, 91) * mm});
            skPoint(sketch, "E68.0", {"position": v(-6.35, 116.66) * mm});
            skPoint(sketch, "E69.0", {"position": v(38.1, 116.66) * mm});
            skPoint(sketch, "E70.0", {"position": v(-6.35, -188.14) * mm});
            skLineSegment(sketch, "E71", {"start": v(38.1, 116.66) * mm, "end": v(-6.35, 91) * mm});
            skLineSegment(sketch, "E72", {"start": v(-6.35, 91) * mm, "end": v(-6.35, 116.66) * mm});
            skLineSegment(sketch, "E73", {"start": v(38.1, 116.66) * mm, "end": v(-6.35, 116.66) * mm});
            skLineSegment(sketch, "E74", {"start": v(-6.35, -188.14) * mm, "end": v(38.1, -162.47) * mm});
            skLineSegment(sketch, "E75", {"start": v(38.1, -162.47) * mm, "end": v(38.1, -188.14) * mm});
            skLineSegment(sketch, "E76", {"start": v(38.1, -188.14) * mm, "end": v(-6.35, -188.14) * mm});
            skSolve(sketch);
        }
        {
            var Q0;
            Q0 = qSketchRegion(id + "F10", true);
            extrude(context, id + "F11", {"entities" : qUnion([Q0]), "operationType" : NewBodyOperationType.REMOVE, "endBound" : BoundingType.THROUGH_ALL, "oppositeDirection" : true, "depth" : 25.4 * mm, "offsetDistance" : 25.4 * mm});
        }
    });
